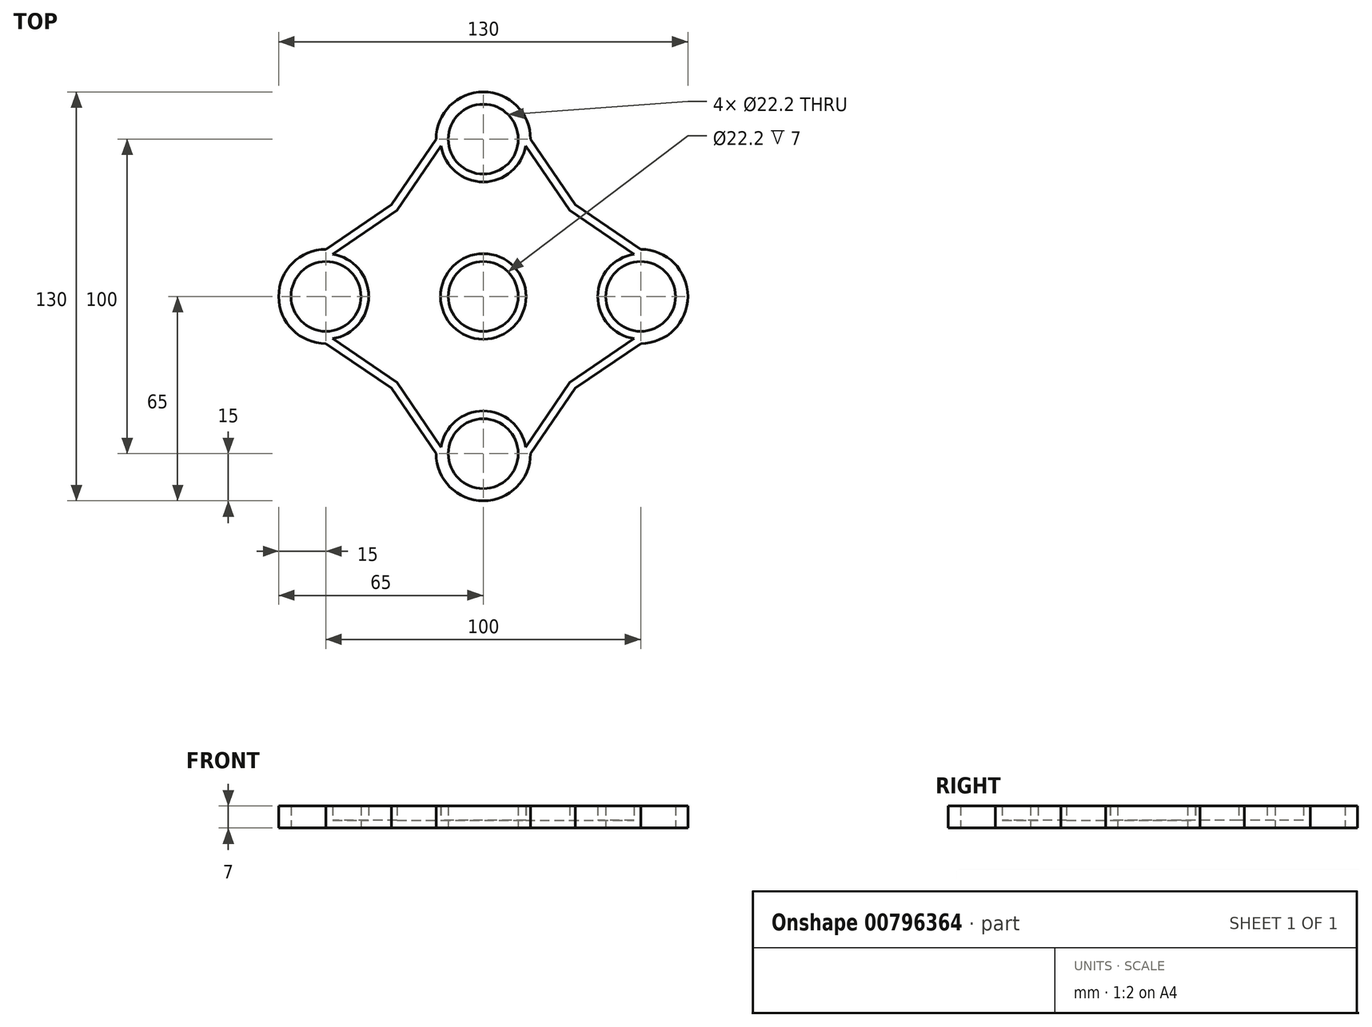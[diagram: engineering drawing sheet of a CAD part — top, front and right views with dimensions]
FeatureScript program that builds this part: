
annotation { "Feature Type Name" : "Feature", "Feature Type Description" : "" }
export const myFeature = defineFeature(function(context is Context, id is Id, definition is map)
    precondition{}
    {
        {
            var Q0;
            Q0=qCreatedBy(makeId("Top.planeOp"),FACE);
            var sketch = newSketch(context, id + "F0", { "sketchPlane" : qUnion([Q0])});
            skCircle(sketch, "E0", {"center": v(0, 50) * mm, "radius": 11.1 * mm});
            skCircle(sketch, "E1.1.0", {"center": v(-50, 0) * mm, "radius": 11.1 * mm});
            skCircle(sketch, "E1.2.0", {"center": v(0, -50) * mm, "radius": 11.1 * mm});
            skCircle(sketch, "E1.3.0", {"center": v(50, 0) * mm, "radius": 11.1 * mm});
            skPoint(sketch, "E1.center", {"position": v(0, 0) * mm});
            skCircle(sketch, "E2", {"center": v(0, 0) * mm, "radius": 11.1 * mm});
            skCircle(sketch, "E3", {"center": v(0, 50) * mm, "radius": 15 * mm});
            skCircle(sketch, "E4.1.0", {"center": v(-50, 0) * mm, "radius": 15 * mm});
            skCircle(sketch, "E4.2.0", {"center": v(0, -50) * mm, "radius": 15 * mm});
            skCircle(sketch, "E4.3.0", {"center": v(50, 0) * mm, "radius": 15 * mm});
            skLineSegment(sketch, "E5", {"start": v(-29.2, -29.16) * mm, "end": v(-50, -15) * mm});
            skLineSegment(sketch, "E6", {"start": v(-29.2, -29.16) * mm, "end": v(-15, -50) * mm});
            skLineSegment(sketch, "E7", {"start": v(-50, 15) * mm, "end": v(-29.2, 29.16) * mm});
            skLineSegment(sketch, "E8", {"start": v(-29.2, 29.16) * mm, "end": v(-15, 50) * mm});
            skLineSegment(sketch, "E9", {"start": v(15, 50) * mm, "end": v(29.2, 29.16) * mm});
            skLineSegment(sketch, "E10", {"start": v(29.2, 29.16) * mm, "end": v(50, 15) * mm});
            skLineSegment(sketch, "E11", {"start": v(15, -50) * mm, "end": v(29.2, -29.16) * mm});
            skLineSegment(sketch, "E12", {"start": v(29.2, -29.16) * mm, "end": v(50, -15) * mm});
            skSolve(sketch);
        }
        {
            var Q0;
            Q0=makeQuery(id+"F0.imprint","IMPRINT",FACE,{"disambiguationData":[TD([[makeQuery(id+"F0.imprint","IMPRINT",EDGE,{"derivedFrom":sQuery(id+"F0.wireOp",EDGE,"E2")}),-1.0]])]});
            var Q1;
            Q1=makeQuery(id+"F0.imprint","IMPRINT",FACE,{"disambiguationData":[TD([[makeQuery(id+"F0.imprint","IMPRINT",EDGE,{"derivedFrom":sQuery(id+"F0.wireOp",EDGE,"E0")}),-1.0]])]});
            var Q2;
            Q2=makeQuery(id+"F0.imprint","IMPRINT",FACE,{"disambiguationData":[TD([[makeQuery(id+"F0.imprint","IMPRINT",EDGE,{"derivedFrom":sQuery(id+"F0.wireOp",EDGE,"E1.3.0")}),-1.0]])]});
            var Q3;
            Q3=makeQuery(id+"F0.imprint","IMPRINT",FACE,{"disambiguationData":[TD([[makeQuery(id+"F0.imprint","IMPRINT",EDGE,{"derivedFrom":sQuery(id+"F0.wireOp",EDGE,"E1.2.0")}),-1.0]])]});
            var Q4;
            Q4=makeQuery(id+"F0.imprint","IMPRINT",FACE,{"disambiguationData":[TD([[makeQuery(id+"F0.imprint","IMPRINT",EDGE,{"derivedFrom":sQuery(id+"F0.wireOp",EDGE,"E1.1.0")}),-1.0]])]});
            extrude(context, id + "F1", {"entities" : qUnion([Q0, Q1, Q2, Q3, Q4]), "endBound" : BoundingType.SYMMETRIC, "depth" : 7 * mm, "offsetDistance" : 25 * mm});
        }
        {
            var Q0;
            Q0=makeQuery(id+"F1.opExtrude","CAP_FACE",FACE,{"disambiguationData":[OSD([sQuery(id+"F0.wireOp",EDGE,"E0"),sQuery(id+"F0.wireOp",EDGE,"E1.1.0"),sQuery(id+"F0.wireOp",EDGE,"E1.2.0"),sQuery(id+"F0.wireOp",EDGE,"E1.3.0"),sQuery(id+"F0.wireOp",EDGE,"E2"),sQuery(id+"F0.wireOp",EDGE,"E3"),sQuery(id+"F0.wireOp",EDGE,"E4.1.0"),sQuery(id+"F0.wireOp",EDGE,"E4.2.0"),sQuery(id+"F0.wireOp",EDGE,"E4.3.0"),sQuery(id+"F0.wireOp",EDGE,"E5"),sQuery(id+"F0.wireOp",EDGE,"E6"),sQuery(id+"F0.wireOp",EDGE,"E7"),sQuery(id+"F0.wireOp",EDGE,"E8"),sQuery(id+"F0.wireOp",EDGE,"E9"),sQuery(id+"F0.wireOp",EDGE,"E10"),sQuery(id+"F0.wireOp",EDGE,"E11"),sQuery(id+"F0.wireOp",EDGE,"E12")])],"isStart":false});
            shell(context, id + "F2", {"entities" : qUnion([Q0]), "thickness" : 2.5 * mm});
        }
    });
